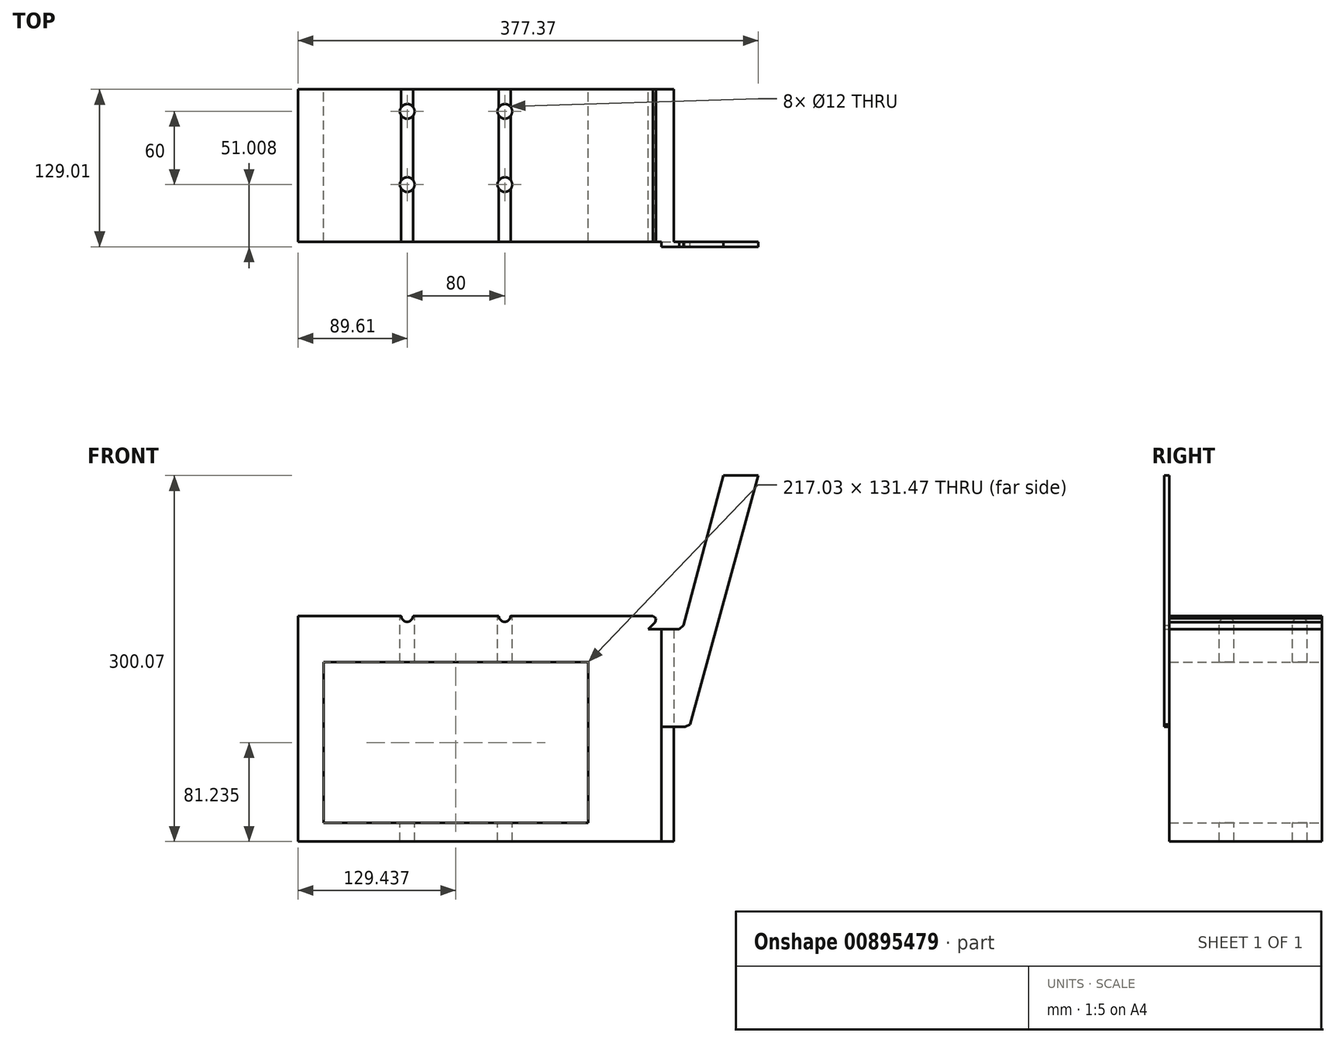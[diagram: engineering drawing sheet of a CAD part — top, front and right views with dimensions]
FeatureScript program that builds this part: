
annotation { "Feature Type Name" : "Feature", "Feature Type Description" : "" }
export const myFeature = defineFeature(function(context is Context, id is Id, definition is map)
    precondition{}
    {
        {
            var Q0;
            Q0=qCreatedBy(makeId("Front.planeOp"),FACE);
            var sketch = newSketch(context, id + "F0", { "sketchPlane" : qUnion([Q0])});
            skLineSegment(sketch, "E0", {"start": v(44.78, 6.67) * mm, "end": v(46.17, 6.67) * mm});
            skLineSegment(sketch, "E1", {"start": v(-49.72, 30.26) * mm, "end": v(-49.72, 20.26) * mm, "construction": true});
            skLineSegment(sketch, "E2", {"start": v(-44.92, 30.26) * mm, "end": v(-44.92, 20.26) * mm, "construction": true});
            skLineSegment(sketch, "E3", {"start": v(-9.7, 30.26) * mm, "end": v(-9.7, 20.26) * mm, "construction": true});
            skLineSegment(sketch, "E4", {"start": v(-4.9, 30.26) * mm, "end": v(-4.9, 20.26) * mm, "construction": true});
            skLineSegment(sketch, "E5", {"start": v(4.75, -2.45) * mm, "end": v(16.58, -6.76) * mm});
            skLineSegment(sketch, "E6", {"start": v(26.98, -18.03) * mm, "end": v(26.98, -19.52) * mm});
            skLineSegment(sketch, "E7", {"start": v(1.78, 1.25) * mm, "end": v(2.37, -0.62) * mm});
            skLineSegment(sketch, "E8", {"start": v(2.37, -0.62) * mm, "end": v(4.75, -2.45) * mm});
            skLineSegment(sketch, "E9", {"start": v(-15.55, 20.26) * mm, "end": v(-9.7, 20.26) * mm});
            skLineSegment(sketch, "E10", {"start": v(-47.32, 12.25) * mm, "end": v(-47.32, 25.13) * mm, "construction": true});
            skLineSegment(sketch, "E11", {"start": v(-7.3, 12.25) * mm, "end": v(-7.3, 25.13) * mm, "construction": true});
            skLineSegment(sketch, "E12", {"start": v(-92.1, -67.3) * mm, "end": v(-92.1, 15.26) * mm});
            skLineSegment(sketch, "E13", {"start": v(-81.6, -3.76) * mm, "end": v(-81.6, -18.02) * mm});
            skLineSegment(sketch, "E14", {"start": v(-81.6, -41.03) * mm, "end": v(-81.6, -59.54) * mm});
            skLineSegment(sketch, "E15", {"start": v(-81.6, -41.03) * mm, "end": v(-81.6, -41.03) * mm});
            skLineSegment(sketch, "E16", {"start": v(-87.1, -72.3) * mm, "end": v(-38.56, -72.3) * mm});
            skLineSegment(sketch, "E17", {"start": v(-15.55, -72.3) * mm, "end": v(44.07, -72.3) * mm});
            skLineSegment(sketch, "E18", {"start": v(-37.56, -69.3) * mm, "end": v(-16.55, -69.3) * mm});
            skLineSegment(sketch, "E19", {"start": v(-76.59, -64.54) * mm, "end": v(21.98, -64.54) * mm});
            skLineSegment(sketch, "E20", {"start": v(-37.56, 19.26) * mm, "end": v(-37.56, 17.26) * mm});
            skLineSegment(sketch, "E21", {"start": v(-37.56, -71.3) * mm, "end": v(-37.56, -69.3) * mm});
            skLineSegment(sketch, "E22", {"start": v(-16.55, 19.26) * mm, "end": v(-16.55, 17.26) * mm});
            skLineSegment(sketch, "E23", {"start": v(-16.55, -71.3) * mm, "end": v(-16.55, -69.3) * mm});
            skLineSegment(sketch, "E24", {"start": v(-82.6, -40.03) * mm, "end": v(-84.6, -40.03) * mm});
            skLineSegment(sketch, "E25", {"start": v(66.71, -25.27) * mm, "end": v(41.49, -25.27) * mm});
            skLineSegment(sketch, "E26", {"start": v(-84.6, -19.02) * mm, "end": v(-82.6, -19.02) * mm});
            skLineSegment(sketch, "E27", {"start": v(51.57, 14.76) * mm, "end": v(54.51, 17.7) * mm});
            skLineSegment(sketch, "E28", {"start": v(1.78, 1.25) * mm, "end": v(-76.59, 1.25) * mm});
            skLineSegment(sketch, "E29", {"start": v(18.97, -6.76) * mm, "end": v(26.69, -14.47) * mm});
            skLineSegment(sketch, "E30", {"start": v(26.98, -59.54) * mm, "end": v(26.98, -41.03) * mm});
            skLineSegment(sketch, "E31", {"start": v(26.98, -41.03) * mm, "end": v(26.98, -19.52) * mm});
            skLineSegment(sketch, "E32", {"start": v(26.98, -18.02) * mm, "end": v(26.98, -15.18) * mm});
            skLineSegment(sketch, "E33", {"start": v(33.98, -17.77) * mm, "end": v(33.98, 12.25) * mm});
            skLineSegment(sketch, "E34", {"start": v(36.48, 14.76) * mm, "end": v(63.62, 14.76) * mm});
            skLineSegment(sketch, "E35", {"start": v(-32.73, 17.26) * mm, "end": v(-21.38, 17.26) * mm});
            skLineSegment(sketch, "E36", {"start": v(-87.1, 20.26) * mm, "end": v(-49.72, 20.26) * mm});
            skLineSegment(sketch, "E37", {"start": v(62, -25.27) * mm, "end": v(62, -67.3) * mm});
            skLineSegment(sketch, "E38", {"start": v(66.04, 16.6) * mm, "end": v(82.47, 77.94) * mm});
            skArc(sketch, "E39", {"start": v(-92.1, -67.3) * mm, "mid": v(-90.63, -70.83) * mm, "end": v(-87.1, -72.3) * mm});
            skArc(sketch, "E40", {"start": v(-81.6, -59.54) * mm, "mid": v(-80.12, -63.08) * mm, "end": v(-76.59, -64.54) * mm});
            skLineSegment(sketch, "E41", {"start": v(-85.26, -36.14) * mm, "end": v(-86.32, -37.02) * mm});
            skLineSegment(sketch, "E42", {"start": v(-86.32, -37.02) * mm, "end": v(-86.56, -38.37) * mm});
            skArc(sketch, "E43", {"start": v(-85.26, -36.14) * mm, "mid": v(-86.32, -37.02) * mm, "end": v(-86.56, -38.37) * mm});
            skLineSegment(sketch, "E44", {"start": v(-86.56, -38.37) * mm, "end": v(-85.88, -39.56) * mm});
            skLineSegment(sketch, "E45", {"start": v(-85.88, -39.56) * mm, "end": v(-84.6, -40.03) * mm});
            skLineSegment(sketch, "E46", {"start": v(-84.6, -19.02) * mm, "end": v(-85.88, -19.49) * mm});
            skLineSegment(sketch, "E47", {"start": v(-85.88, -19.49) * mm, "end": v(-86.56, -20.68) * mm});
            skArc(sketch, "E48", {"start": v(-84.6, -19.02) * mm, "mid": v(-85.88, -19.49) * mm, "end": v(-86.56, -20.68) * mm});
            skLineSegment(sketch, "E49", {"start": v(-86.56, -20.68) * mm, "end": v(-86.32, -22.03) * mm});
            skLineSegment(sketch, "E50", {"start": v(-86.32, -22.03) * mm, "end": v(-85.26, -22.9) * mm});
            skLineSegment(sketch, "E51", {"start": v(-38.56, -72.3) * mm, "end": v(-37.86, -72) * mm});
            skLineSegment(sketch, "E52", {"start": v(-37.86, -72) * mm, "end": v(-37.56, -71.3) * mm});
            skLineSegment(sketch, "E53", {"start": v(-16.55, -71.3) * mm, "end": v(-16.26, -72) * mm});
            skLineSegment(sketch, "E54", {"start": v(-16.26, -72) * mm, "end": v(-15.55, -72.3) * mm});
            skLineSegment(sketch, "E55", {"start": v(-85.26, -36.14) * mm, "end": v(-84.6, -35.2) * mm});
            skLineSegment(sketch, "E56", {"start": v(-84.6, -23.85) * mm, "end": v(-85.26, -22.9) * mm});
            skLineSegment(sketch, "E57", {"start": v(-82.6, -19.02) * mm, "end": v(-81.88, -18.72) * mm});
            skLineSegment(sketch, "E58", {"start": v(-81.88, -18.72) * mm, "end": v(-81.6, -18.02) * mm});
            skLineSegment(sketch, "E59", {"start": v(-81.6, -41.03) * mm, "end": v(-81.88, -40.32) * mm});
            skLineSegment(sketch, "E60", {"start": v(-81.88, -40.32) * mm, "end": v(-82.6, -40.03) * mm});
            skArc(sketch, "E61", {"start": v(-87.1, 20.26) * mm, "mid": v(-90.63, 18.8) * mm, "end": v(-92.1, 15.26) * mm});
            skArc(sketch, "E62", {"start": v(-76.59, 1.25) * mm, "mid": v(-80.12, -0.22) * mm, "end": v(-81.59, -3.76) * mm});
            skLineSegment(sketch, "E63", {"start": v(-20.44, 16.59) * mm, "end": v(-19.56, 15.53) * mm});
            skLineSegment(sketch, "E64", {"start": v(-19.56, 15.53) * mm, "end": v(-18.21, 15.28) * mm});
            skLineSegment(sketch, "E65", {"start": v(-18.21, 15.28) * mm, "end": v(-17.02, 15.97) * mm});
            skLineSegment(sketch, "E66", {"start": v(-17.02, 15.97) * mm, "end": v(-16.55, 17.26) * mm});
            skLineSegment(sketch, "E67", {"start": v(-37.56, 17.26) * mm, "end": v(-37.1, 15.97) * mm});
            skLineSegment(sketch, "E68", {"start": v(-37.1, 15.97) * mm, "end": v(-35.9, 15.28) * mm});
            skLineSegment(sketch, "E69", {"start": v(-35.9, 15.28) * mm, "end": v(-34.55, 15.53) * mm});
            skLineSegment(sketch, "E70", {"start": v(-34.55, 15.53) * mm, "end": v(-33.67, 16.59) * mm});
            skLineSegment(sketch, "E71", {"start": v(-15.55, 20.26) * mm, "end": v(-16.26, 19.97) * mm});
            skLineSegment(sketch, "E72", {"start": v(-16.26, 19.97) * mm, "end": v(-16.55, 19.26) * mm});
            skLineSegment(sketch, "E73", {"start": v(-20.44, 16.59) * mm, "end": v(-21.38, 17.26) * mm});
            skLineSegment(sketch, "E74", {"start": v(-32.73, 17.26) * mm, "end": v(-33.67, 16.59) * mm});
            skLineSegment(sketch, "E75", {"start": v(-37.56, 19.26) * mm, "end": v(-37.86, 19.97) * mm});
            skLineSegment(sketch, "E76", {"start": v(-37.86, 19.97) * mm, "end": v(-38.56, 20.26) * mm});
            skArc(sketch, "E77", {"start": v(21.98, -64.54) * mm, "mid": v(25.51, -63.08) * mm, "end": v(26.98, -59.54) * mm});
            skLineSegment(sketch, "E78", {"start": v(26.98, -15.18) * mm, "end": v(26.69, -14.47) * mm});
            skArc(sketch, "E79", {"start": v(33.98, -17.77) * mm, "mid": v(36.18, -23.07) * mm, "end": v(41.49, -25.27) * mm});
            skArc(sketch, "E80", {"start": v(57, -72.3) * mm, "mid": v(60.53, -70.83) * mm, "end": v(62, -67.3) * mm});
            skLineSegment(sketch, "E81", {"start": v(66.71, -25.27) * mm, "end": v(67.86, -25) * mm});
            skLineSegment(sketch, "E82", {"start": v(67.86, -25) * mm, "end": v(68.75, -24.22) * mm});
            skLineSegment(sketch, "E83", {"start": v(36.48, 14.76) * mm, "end": v(34.72, 14.02) * mm});
            skLineSegment(sketch, "E84", {"start": v(34.72, 14.02) * mm, "end": v(33.98, 12.25) * mm});
            skLineSegment(sketch, "E85", {"start": v(63.62, 14.76) * mm, "end": v(65.15, 15.27) * mm});
            skLineSegment(sketch, "E86", {"start": v(65.15, 15.27) * mm, "end": v(66.04, 16.6) * mm});
            skLineSegment(sketch, "E87", {"start": v(54.84, 19.33) * mm, "end": v(54.51, 17.7) * mm});
            skLineSegment(sketch, "E88", {"start": v(54.51, 17.7) * mm, "end": v(54.84, 19.33) * mm});
            skLineSegment(sketch, "E89", {"start": v(53.45, 20.26) * mm, "end": v(54.84, 19.33) * mm});
            skCircle(sketch, "E90", {"center": v(46.49, 2.25) * mm, "radius": 4.5 * mm});
            skLineSegment(sketch, "E91", {"start": v(57, -72.3) * mm, "end": v(44.07, -72.3) * mm});
            skLineSegment(sketch, "E92", {"start": v(82.47, 77.94) * mm, "end": v(96.58, 77.94) * mm});
            skLineSegment(sketch, "E93", {"start": v(96.58, 77.94) * mm, "end": v(68.75, -24.22) * mm});
            skLineSegment(sketch, "E94", {"start": v(16.58, -6.76) * mm, "end": v(18.97, -6.76) * mm});
            skLineSegment(sketch, "E95", {"start": v(-84.6, -35.2) * mm, "end": v(-84.6, -23.85) * mm});
            skArc(sketch, "E96", {"start": v(-49.72, 20.26) * mm, "mid": v(-47.32, 17.86) * mm, "end": v(-44.92, 20.26) * mm});
            skArc(sketch, "E97", {"start": v(-9.7, 20.26) * mm, "mid": v(-7.3, 17.86) * mm, "end": v(-4.9, 20.26) * mm});
            skLineSegment(sketch, "E98.trimOffspring", {"start": v(-44.92, 20.26) * mm, "end": v(-38.56, 20.26) * mm});
            skLineSegment(sketch, "E99.trimOffspring", {"start": v(-4.9, 20.26) * mm, "end": v(53.45, 20.26) * mm});
            skLineSegment(sketch, "E100.trimOffspring", {"start": v(-4.9, 20.26) * mm, "end": v(15.22, 20.26) * mm});
            skSolve(sketch);
        }
        {
            var Q0;
            Q0=qCreatedBy(makeId("Front.planeOp"),FACE);
            var sketch = newSketch(context, id + "F1", { "sketchPlane" : qUnion([Q0])});
            skLineSegment(sketch, "E101.0", {"start": v(-92.1, -67.3) * mm, "end": v(-92.1, 15.26) * mm});
            skLineSegment(sketch, "E101.1", {"start": v(-87.1, 20.26) * mm, "end": v(-49.72, 20.26) * mm});
            skLineSegment(sketch, "E101.2", {"start": v(-4.9, 20.26) * mm, "end": v(53.45, 20.26) * mm});
            skLineSegment(sketch, "E101.3", {"start": v(53.45, 20.26) * mm, "end": v(54.84, 19.33) * mm});
            skLineSegment(sketch, "E101.4", {"start": v(54.84, 19.33) * mm, "end": v(54.51, 17.7) * mm});
            skLineSegment(sketch, "E101.5", {"start": v(51.57, 14.76) * mm, "end": v(54.51, 17.7) * mm});
            skLineSegment(sketch, "E101.6", {"start": v(62, -25.27) * mm, "end": v(62, -67.3) * mm});
            skLineSegment(sketch, "E101.7", {"start": v(-15.55, -72.3) * mm, "end": v(44.07, -72.3) * mm});
            skLineSegment(sketch, "E101.8", {"start": v(-37.56, -69.3) * mm, "end": v(-16.55, -69.3) * mm});
            skLineSegment(sketch, "E101.9", {"start": v(-87.1, -72.3) * mm, "end": v(-38.56, -72.3) * mm});
            skLineSegment(sketch, "E101.10", {"start": v(-81.6, -3.76) * mm, "end": v(-81.6, -18.02) * mm});
            skLineSegment(sketch, "E101.11", {"start": v(26.98, -41.03) * mm, "end": v(26.98, -19.52) * mm});
            skLineSegment(sketch, "E101.12", {"start": v(-76.59, -64.54) * mm, "end": v(21.98, -64.54) * mm});
            skLineSegment(sketch, "E101.13", {"start": v(1.78, 1.25) * mm, "end": v(-76.59, 1.25) * mm});
            skLineSegment(sketch, "E101.14", {"start": v(-32.73, 17.26) * mm, "end": v(-21.38, 17.26) * mm});
            skArc(sketch, "E101.15", {"start": v(-49.72, 20.26) * mm, "mid": v(-47.32, 17.86) * mm, "end": v(-44.92, 20.26) * mm});
            skArc(sketch, "E101.16", {"start": v(-9.7, 20.26) * mm, "mid": v(-7.3, 17.86) * mm, "end": v(-4.9, 20.26) * mm});
            skLineSegment(sketch, "E101.17", {"start": v(-15.55, 20.26) * mm, "end": v(-9.7, 20.26) * mm});
            skLineSegment(sketch, "E101.18", {"start": v(-44.92, 20.26) * mm, "end": v(-38.56, 20.26) * mm});
            skArc(sketch, "E101.19", {"start": v(-92.1, -67.3) * mm, "mid": v(-90.63, -70.83) * mm, "end": v(-87.1, -72.3) * mm});
            skLineSegment(sketch, "E102", {"start": v(-92.1, 15.26) * mm, "end": v(-87.1, 20.26) * mm});
            skLineSegment(sketch, "E103", {"start": v(-38.56, 20.26) * mm, "end": v(-32.73, 17.26) * mm});
            skLineSegment(sketch, "E104", {"start": v(-15.55, 20.26) * mm, "end": v(-21.38, 17.26) * mm});
            skLineSegment(sketch, "E105", {"start": v(51.57, 14.76) * mm, "end": v(36.45, 15.23) * mm});
            skLineSegment(sketch, "E106", {"start": v(36.45, 15.23) * mm, "end": v(33.68, 12.46) * mm});
            skLineSegment(sketch, "E107", {"start": v(33.68, 12.46) * mm, "end": v(33.68, -17.8) * mm});
            skLineSegment(sketch, "E108", {"start": v(33.68, -17.8) * mm, "end": v(41.17, -25.29) * mm});
            skLineSegment(sketch, "E109", {"start": v(41.17, -25.29) * mm, "end": v(62, -25.27) * mm});
            skLineSegment(sketch, "E110", {"start": v(62, -67.3) * mm, "end": v(56.9, -72.4) * mm});
            skLineSegment(sketch, "E111", {"start": v(56.9, -72.4) * mm, "end": v(44.07, -72.3) * mm});
            skLineSegment(sketch, "E112", {"start": v(-15.55, -72.3) * mm, "end": v(-16.55, -69.3) * mm});
            skLineSegment(sketch, "E113", {"start": v(-37.56, -69.3) * mm, "end": v(-38.56, -72.3) * mm});
            skLineSegment(sketch, "E114", {"start": v(-76.59, -64.54) * mm, "end": v(-81.63, -59.5) * mm});
            skLineSegment(sketch, "E115", {"start": v(-81.63, -59.5) * mm, "end": v(-81.63, -41.15) * mm});
            skLineSegment(sketch, "E116", {"start": v(-81.63, -41.15) * mm, "end": v(-84.8, -35.17) * mm});
            skLineSegment(sketch, "E117", {"start": v(-84.8, -35.17) * mm, "end": v(-84.8, -23.48) * mm});
            skLineSegment(sketch, "E118", {"start": v(-84.8, -23.48) * mm, "end": v(-81.6, -18.02) * mm});
            skLineSegment(sketch, "E119", {"start": v(-81.6, -3.76) * mm, "end": v(-76.59, 1.25) * mm});
            skLineSegment(sketch, "E120", {"start": v(1.78, 1.25) * mm, "end": v(18.87, -6.72) * mm});
            skLineSegment(sketch, "E121", {"start": v(18.87, -6.72) * mm, "end": v(26.98, -19.52) * mm});
            skLineSegment(sketch, "E122", {"start": v(21.98, -64.54) * mm, "end": v(26.98, -59.54) * mm});
            skLineSegment(sketch, "E123", {"start": v(26.98, -59.54) * mm, "end": v(26.98, -41.03) * mm});
            skLineSegment(sketch, "E124", {"start": v(51.57, 14.76) * mm, "end": v(64.33, 14.76) * mm});
            skLineSegment(sketch, "E125", {"start": v(64.33, 14.76) * mm, "end": v(66.05, 16.47) * mm});
            skLineSegment(sketch, "E126", {"start": v(66.05, 16.47) * mm, "end": v(82.38, 77.86) * mm});
            skLineSegment(sketch, "E127", {"start": v(82.38, 77.86) * mm, "end": v(96.74, 77.86) * mm});
            skLineSegment(sketch, "E128", {"start": v(96.74, 77.86) * mm, "end": v(68.67, -24.25) * mm});
            skLineSegment(sketch, "E129", {"start": v(68.67, -24.25) * mm, "end": v(66.73, -25.27) * mm});
            skLineSegment(sketch, "E130", {"start": v(66.73, -25.27) * mm, "end": v(62, -25.27) * mm});
            skSolve(sketch);
        }
        {
            var Q0;
            Q0=qCreatedBy(makeId("Front.planeOp"),FACE);
            var sketch = newSketch(context, id + "F2", { "sketchPlane" : qUnion([Q0])});
            skPoint(sketch, "E131.0", {"position": v(-87.1, 20.26) * mm});
            skPoint(sketch, "E131.1", {"position": v(-92.1, 15.26) * mm});
            skPoint(sketch, "E131.2", {"position": v(-87.1, -72.3) * mm});
            skPoint(sketch, "E131.3", {"position": v(-92.1, -67.3) * mm});
            skPoint(sketch, "E131.4", {"position": v(62, -67.3) * mm});
            skPoint(sketch, "E131.5", {"position": v(53.45, 20.26) * mm});
            skPoint(sketch, "E131.6", {"position": v(54.84, 19.33) * mm});
            skPoint(sketch, "E131.7", {"position": v(54.51, 17.7) * mm});
            skArc(sketch, "E131.8", {"start": v(-9.7, 20.26) * mm, "mid": v(-7.3, 17.86) * mm, "end": v(-4.9, 20.26) * mm});
            skArc(sketch, "E131.9", {"start": v(-49.72, 20.26) * mm, "mid": v(-47.32, 17.86) * mm, "end": v(-44.92, 20.26) * mm});
            skLineSegment(sketch, "E131.10", {"start": v(-76.59, -64.54) * mm, "end": v(21.98, -64.54) * mm});
            skLineSegment(sketch, "E131.11", {"start": v(1.78, 1.25) * mm, "end": v(-76.59, 1.25) * mm});
            skLineSegment(sketch, "E131.12", {"start": v(-81.63, -59.5) * mm, "end": v(-81.63, -41.15) * mm});
            skLineSegment(sketch, "E131.13", {"start": v(26.98, -41.03) * mm, "end": v(26.98, -19.52) * mm});
            skLineSegment(sketch, "E132.bottom", {"start": v(-92.1, 20.26) * mm, "end": v(-49.72, 20.26) * mm});
            skLineSegment(sketch, "E132.top", {"start": v(-92.1, -72.3) * mm, "end": v(62, -72.3) * mm});
            skLineSegment(sketch, "E132.left", {"start": v(-92.1, 20.26) * mm, "end": v(-92.1, -72.3) * mm});
            skLineSegment(sketch, "E132.right", {"start": v(62, 14.76) * mm, "end": v(62, -72.3) * mm});
            skLineSegment(sketch, "E133.0", {"start": v(53.45, 20.26) * mm, "end": v(54.84, 19.33) * mm});
            skLineSegment(sketch, "E133.1", {"start": v(54.84, 19.33) * mm, "end": v(54.51, 17.7) * mm});
            skLineSegment(sketch, "E133.2", {"start": v(51.57, 14.76) * mm, "end": v(54.51, 17.7) * mm});
            skLineSegment(sketch, "E133.3", {"start": v(51.57, 14.76) * mm, "end": v(62, 14.76) * mm});
            skPoint(sketch, "E134.orphan", {"position": v(64.33, 14.76) * mm});
            skLineSegment(sketch, "E135.trimOffspring", {"start": v(-4.9, 20.26) * mm, "end": v(53.45, 20.26) * mm});
            skLineSegment(sketch, "E136.trimOffspring", {"start": v(-44.92, 20.26) * mm, "end": v(-9.7, 20.26) * mm});
            skLineSegment(sketch, "E137.bottom", {"start": v(-81.63, 1.25) * mm, "end": v(26.98, 1.25) * mm});
            skLineSegment(sketch, "E137.top", {"start": v(-81.63, -64.54) * mm, "end": v(26.98, -64.54) * mm});
            skLineSegment(sketch, "E137.left", {"start": v(-81.63, 1.25) * mm, "end": v(-81.63, -64.54) * mm});
            skLineSegment(sketch, "E137.right", {"start": v(26.98, 1.25) * mm, "end": v(26.98, -64.54) * mm});
            skSolve(sketch);
        }
        {
            var Q0;
            Q0 = qSketchRegion(id + "F2", true);
            extrude(context, id + "F3", {"entities" : qUnion([Q0]), "endBound" : BoundingType.SYMMETRIC, "depth" : 62.56 * mm, "offsetDistance" : 25 * mm});
        }
        {
            var Q0;
            Q0=makeQuery(id+"F3.opExtrude","CAP_FACE",FACE,{"disambiguationData":[OSD([sQuery(id+"F2.wireOp",EDGE,"E131.8"),sQuery(id+"F2.wireOp",EDGE,"E131.9"),sQuery(id+"F2.wireOp",EDGE,"E132.bottom"),sQuery(id+"F2.wireOp",EDGE,"E132.top"),sQuery(id+"F2.wireOp",EDGE,"E132.left"),sQuery(id+"F2.wireOp",EDGE,"E132.right"),sQuery(id+"F2.wireOp",EDGE,"E133.0"),sQuery(id+"F2.wireOp",EDGE,"E133.1"),sQuery(id+"F2.wireOp",EDGE,"E133.2"),sQuery(id+"F2.wireOp",EDGE,"E133.3"),sQuery(id+"F2.wireOp",EDGE,"E135.trimOffspring"),sQuery(id+"F2.wireOp",EDGE,"E136.trimOffspring"),sQuery(id+"F2.wireOp",EDGE,"E137.bottom"),sQuery(id+"F2.wireOp",EDGE,"E137.top"),sQuery(id+"F2.wireOp",EDGE,"E137.left"),sQuery(id+"F2.wireOp",EDGE,"E137.right")])],"isStart":false});
            var sketch = newSketch(context, id + "F4", { "sketchPlane" : qUnion([Q0])});
            skLineSegment(sketch, "E138.0", {"start": v(82.38, 77.86) * mm, "end": v(96.74, 77.86) * mm});
            skLineSegment(sketch, "E138.1", {"start": v(66.05, 16.47) * mm, "end": v(82.38, 77.86) * mm});
            skLineSegment(sketch, "E138.2", {"start": v(96.74, 77.86) * mm, "end": v(68.67, -24.25) * mm});
            skLineSegment(sketch, "E138.3", {"start": v(64.33, 14.76) * mm, "end": v(66.05, 16.47) * mm});
            skLineSegment(sketch, "E138.4", {"start": v(57, 14.76) * mm, "end": v(64.33, 14.76) * mm});
            skLineSegment(sketch, "E138.5", {"start": v(66.73, -25.27) * mm, "end": v(62, -25.27) * mm});
            skLineSegment(sketch, "E138.6", {"start": v(68.67, -24.25) * mm, "end": v(66.73, -25.27) * mm});
            skLineSegment(sketch, "E139", {"start": v(62, -25.27) * mm, "end": v(57, -25.27) * mm});
            skLineSegment(sketch, "E140", {"start": v(57, -25.27) * mm, "end": v(57, 14.76) * mm});
            skPoint(sketch, "E141.orphan", {"position": v(51.57, 14.76) * mm});
            skSolve(sketch);
        }
        {
            var Q0;
            Q0 = qSketchRegion(id + "F4", true);
            extrude(context, id + "F5", {"entities" : qUnion([Q0]), "operationType" : NewBodyOperationType.ADD, "depth" : 2 * mm, "offsetDistance" : 25 * mm});
        }
        {
            var Q0;
            Q0=makeQuery(id+"F3.opExtrude","SWEPT_BODY",BODY,{"disambiguationData":[OSD([sQuery(id+"F2.wireOp",EDGE,"E131.8"),sQuery(id+"F2.wireOp",EDGE,"E131.9"),sQuery(id+"F2.wireOp",EDGE,"E132.bottom"),sQuery(id+"F2.wireOp",EDGE,"E132.top"),sQuery(id+"F2.wireOp",EDGE,"E132.left"),sQuery(id+"F2.wireOp",EDGE,"E132.right"),sQuery(id+"F2.wireOp",EDGE,"E133.0"),sQuery(id+"F2.wireOp",EDGE,"E133.1"),sQuery(id+"F2.wireOp",EDGE,"E133.2"),sQuery(id+"F2.wireOp",EDGE,"E133.3"),sQuery(id+"F2.wireOp",EDGE,"E135.trimOffspring"),sQuery(id+"F2.wireOp",EDGE,"E136.trimOffspring"),sQuery(id+"F2.wireOp",EDGE,"E137.bottom"),sQuery(id+"F2.wireOp",EDGE,"E137.top"),sQuery(id+"F2.wireOp",EDGE,"E137.left"),sQuery(id+"F2.wireOp",EDGE,"E137.right")])]});
            var Q1;
            Q1=qCreatedBy(makeId("Origin.pointOp"),VERTEX);
            transform(context, id + "F6", {"entities" : qUnion([Q0]), "transformType" : TransformType.SCALE_UNIFORMLY, "scale" : 2, "scalePoint" : qUnion([Q1]), "makeCopy" : false});
        }
        {
            var Q0;
            Q0=makeQuery(id+"F3.opExtrude","SWEPT_FACE",FACE,{"disambiguationData":[OSD([sQuery(id+"F2.wireOp",EDGE,"E132.bottom")])]});
            var sketch = newSketch(context, id + "F7", { "sketchPlane" : qUnion([Q0])});
            skCircle(sketch, "E142", {"center": v(-94.43, 44.5) * mm, "radius": 6 * mm});
            skCircle(sketch, "E143", {"center": v(-14.43, 44.5) * mm, "radius": 6 * mm});
            skCircle(sketch, "E144", {"center": v(-14.43, -15.5) * mm, "radius": 6 * mm});
            skCircle(sketch, "E145", {"center": v(-94.43, -15.5) * mm, "radius": 6 * mm});
            skSolve(sketch);
        }
        {
            var Q0;
            Q0 = qSketchRegion(id + "F7", true);
            var Q1;
            Q1=makeQuery(id+"F3.opExtrude","SWEPT_FACE",FACE,{"disambiguationData":[OSD([sQuery(id+"F2.wireOp",EDGE,"E137.bottom")])]});
            extrude(context, id + "F8", {"entities" : qUnion([Q0]), "operationType" : NewBodyOperationType.REMOVE, "endBound" : BoundingType.THROUGH_ALL, "oppositeDirection" : true, "depth" : 25 * mm, "endBoundEntityFace" : qUnion([Q1]), "offsetDistance" : 25 * mm});
        }
        {
            var Q0;
            Q0=makeQuery(id+"F3.opExtrude","SWEPT_FACE",FACE,{"disambiguationData":[OSD([sQuery(id+"F2.wireOp",EDGE,"E132.top")])]});
            var sketch = newSketch(context, id + "F9", { "sketchPlane" : qUnion([Q0])});
            skLineSegment(sketch, "E146.bottom", {"start": v(-184.04, 62.5) * mm, "end": v(113.9, 62.5) * mm});
            skLineSegment(sketch, "E146.top", {"start": v(-184.04, 62.5) * mm, "end": v(113.9, 62.5) * mm});
            skLineSegment(sketch, "E146.left", {"start": v(-184.04, 62.5) * mm, "end": v(-184.04, 62.5) * mm});
            skLineSegment(sketch, "E146.right", {"start": v(113.9, 62.5) * mm, "end": v(113.9, 62.5) * mm});
            skSolve(sketch);
        }
        {
            var Q0;
            Q0 = qSketchRegion(id + "F9", true);
            extrude(context, id + "F10", {"entities" : qUnion([Q0]), "operationType" : NewBodyOperationType.REMOVE, "endBound" : BoundingType.THROUGH_ALL, "oppositeDirection" : true, "depth" : 25 * mm, "offsetDistance" : 25 * mm});
        }
    });
